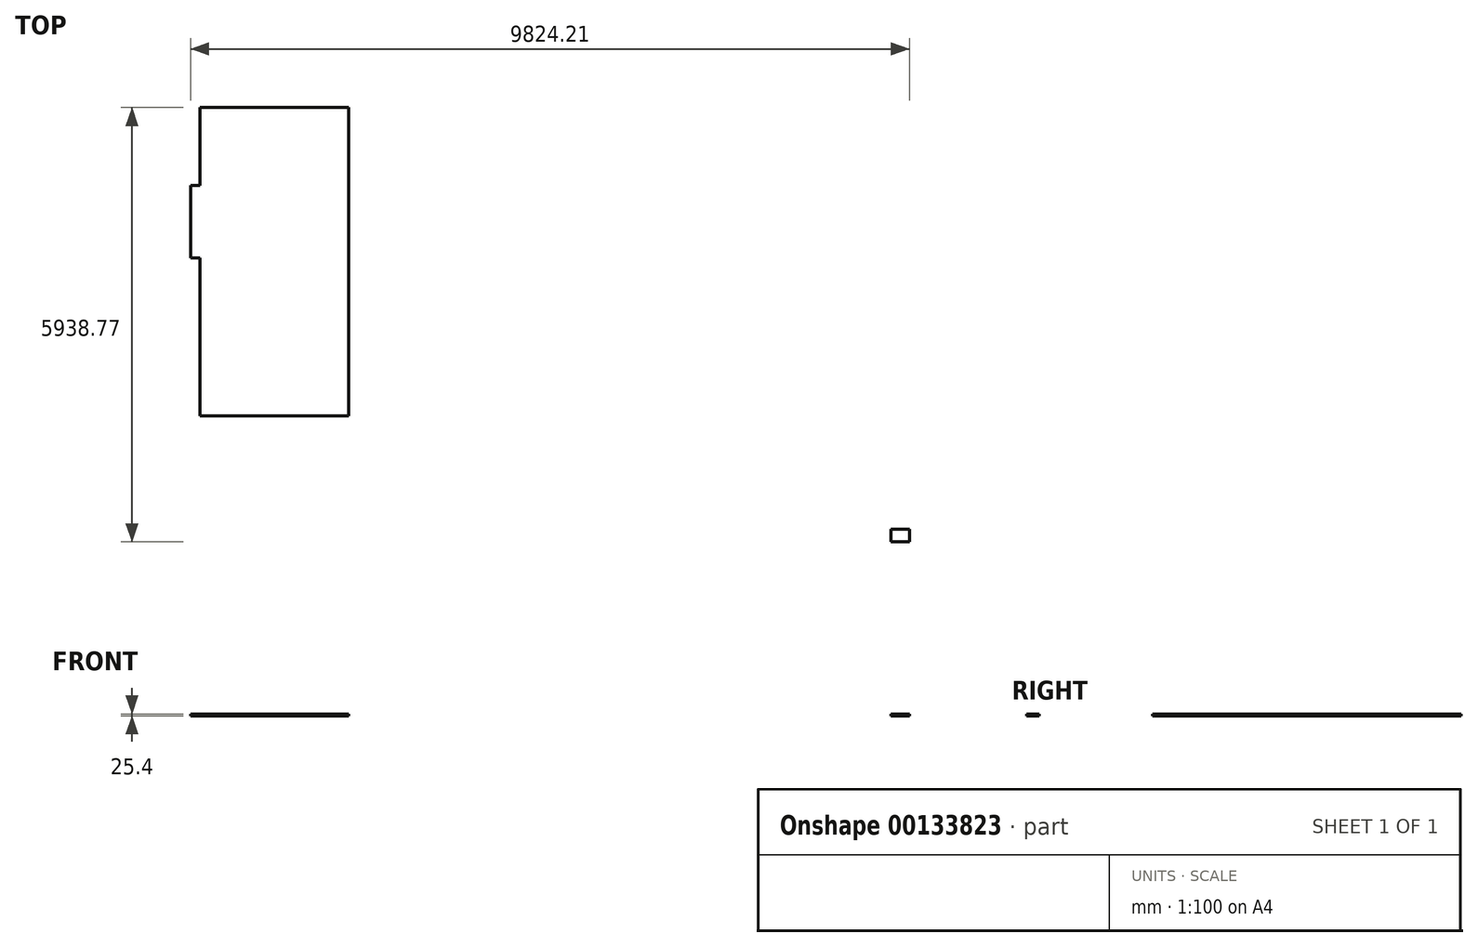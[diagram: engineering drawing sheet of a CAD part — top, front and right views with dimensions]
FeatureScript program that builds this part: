
annotation { "Feature Type Name" : "Feature", "Feature Type Description" : "" }
export const myFeature = defineFeature(function(context is Context, id is Id, definition is map)
    precondition{}
    {
        {
            var Q0;
            Q0=qCreatedBy(makeId("Top.planeOp"),FACE);
            var sketch = newSketch(context, id + "F0", { "sketchPlane" : qUnion([Q0])});
            skLineSegment(sketch, "E0.bottom", {"start": v(-2107.37, -1051.75) * mm, "end": v(1461.33, -1051.75) * mm});
            skLineSegment(sketch, "E0.top", {"start": v(-2107.37, 3164.65) * mm, "end": v(1461.33, 3164.65) * mm});
            skLineSegment(sketch, "E0.left", {"start": v(-2107.37, -1051.75) * mm, "end": v(-2107.37, 3164.65) * mm});
            skLineSegment(sketch, "E0.right", {"start": v(1461.33, -1051.75) * mm, "end": v(1461.33, 3164.65) * mm});
            skLineSegment(sketch, "E1.bottom", {"start": v(-2107.37, 3164.65) * mm, "end": v(-1891.47, 3164.65) * mm});
            skLineSegment(sketch, "E1.top", {"start": v(-2107.37, 2967.8) * mm, "end": v(-1891.47, 2967.8) * mm});
            skLineSegment(sketch, "E1.left", {"start": v(-2107.37, 3164.65) * mm, "end": v(-2107.37, 2967.8) * mm});
            skLineSegment(sketch, "E1.right", {"start": v(-1891.47, 3164.65) * mm, "end": v(-1891.47, 2967.8) * mm});
            skLineSegment(sketch, "E2.bottom", {"start": v(-2107.37, -1051.75) * mm, "end": v(-1852.91, -1051.75) * mm});
            skLineSegment(sketch, "E2.top", {"start": v(-2107.37, -880.3) * mm, "end": v(-1852.91, -880.3) * mm});
            skLineSegment(sketch, "E2.left", {"start": v(-2107.37, -1051.75) * mm, "end": v(-2107.37, -880.3) * mm});
            skLineSegment(sketch, "E2.right", {"start": v(-1852.91, -1051.75) * mm, "end": v(-1852.91, -880.3) * mm});
            skLineSegment(sketch, "E3.left", {"start": v(1461.33, 2097.85) * mm, "end": v(1461.33, 1107.25) * mm});
            skLineSegment(sketch, "E4.bottom", {"start": v(-11677.12, 3820.22) * mm, "end": v(-11550.12, 3820.22) * mm});
            skLineSegment(sketch, "E4.top", {"start": v(-11677.12, 2829.62) * mm, "end": v(-11550.12, 2829.62) * mm});
            skLineSegment(sketch, "E4.right", {"start": v(-11550.12, 3820.22) * mm, "end": v(-11550.12, 2829.62) * mm});
            skLineSegment(sketch, "E5.bottom", {"start": v(-11550.12, 4887.02) * mm, "end": v(-9518.12, 4887.02) * mm});
            skLineSegment(sketch, "E5.top", {"start": v(-11550.12, 670.62) * mm, "end": v(-9518.12, 670.62) * mm});
            skLineSegment(sketch, "E5.left", {"start": v(-11550.12, 4887.02) * mm, "end": v(-11550.12, 670.62) * mm});
            skLineSegment(sketch, "E5.right", {"start": v(-9518.12, 4887.02) * mm, "end": v(-9518.12, 670.62) * mm});
            skLineSegment(sketch, "E6", {"start": v(-11677.12, 3820.22) * mm, "end": v(-11677.12, 2829.62) * mm});
            skSolve(sketch);
        }
        {
            var Q0;
            {var subQ1=sQuery(id+"F0.wireOp",EDGE,"E0.bottom");Q0=makeQuery(id+"F0.imprint","IMPRINT",FACE,{"disambiguationData":[TD([[makeQuery(id+"F0.imprint","IMPRINT",EDGE,{"derivedFrom":subQ1}),1.0]])]});}
            extrude(context, id + "F1", {"entities" : qUnion([Q0]), "depth" : 25.4 * mm});
        }
        {
            var Q0;
            {var subQ3=sQuery(id+"F0.wireOp",EDGE,"E5.bottom");Q0=makeQuery(id+"F0.imprint","IMPRINT",FACE,{"disambiguationData":[TD([[makeQuery(id+"F0.imprint","IMPRINT",EDGE,{"derivedFrom":subQ3}),-1.0]])]});}
            var Q1;
            {var subQ0=sQuery(id+"F0.wireOp",EDGE,"E4.bottom");Q1=makeQuery(id+"F0.imprint","IMPRINT",FACE,{"disambiguationData":[TD([[makeQuery(id+"F0.imprint","IMPRINT",EDGE,{"derivedFrom":subQ0}),-1.0]])]});}
            extrude(context, id + "F2", {"entities" : qUnion([Q0, Q1]), "depth" : 25.4 * mm});
        }
    });
